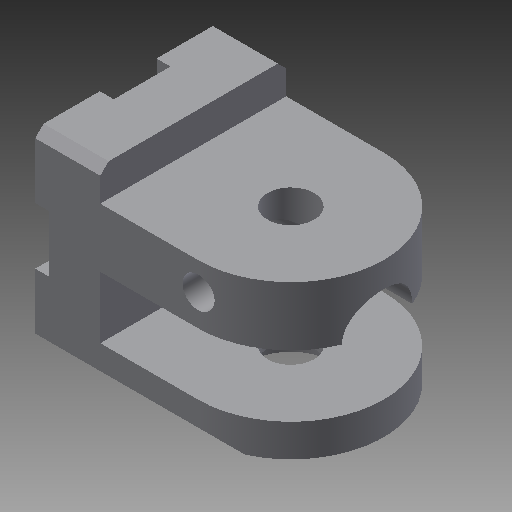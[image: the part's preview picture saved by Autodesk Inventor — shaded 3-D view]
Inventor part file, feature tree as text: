
AUTODESK INVENTOR PART (.ipt)
format: ipt  version: 2018 (Build 220112000, 112)  size: 198,656 bytes
history: native  units: mm
features: other x21, sketch x13, extrude x11, hole x2
ambient origin geometry x8: Origin, YZ Plane, XZ Plane, XY Plane, X Axis, Y Axis, Z Axis, Center Point
bodies: Solid1 (feature_tree)
feature tree (47):
  extrude  "Extrusion1"  Depth=40.0mm TaperAngle=0.0deg
  extrude  "Extrusion2"  Depth=47.5mm TaperAngle=0.0deg
  extrude  "Extrusion3"  Depth=8.4mm TaperAngle=0.0deg
  extrude  "Extrusion4"  Depth=55.0mm TaperAngle=0.0deg
  hole  "Drilling 2"  [1 undecoded]
  extrude  "Extrusion5"  Depth=10.0mm TaperAngle=0.0deg
  extrude  "Extrusion6"  [1 undecoded]
  extrude  "Extrusion7"  [1 undecoded]
  extrude  "Extrusion8"  [1 undecoded]
  extrude  "Extrusion9"  [1 undecoded]
  hole  "Drilling 3"  [1 undecoded]
  extrude  "Extrusion10"  [1 undecoded]
  extrude  "Extrusion11"  [1 undecoded]
  other  "re_XY"
  other  "re_YZ"
  other  "re_ZX"
  other  "re_X"
  other  "re_Y"
  other  "re_Z"
  other  "re_Center"
  other  "bo1_XY"
  other  "bo1_YZ"
  other  "bo1_ZX"
  other  "bo1_X"
  other  "bo1_Y"
  other  "bo1_Z"
  other  "bo1_Center"
  other  "hebel_XY"
  other  "hebel_YZ"
  other  "hebel_ZX"
  other  "hebel_X"
  other  "hebel_Y"
  other  "hebel_Z"
  other  "hebel_Center"
  sketch  "Skizze_1"  dims[d0=40.0mm d1=0.0mm d2=40.0mm d3=0.0mm]
  sketch  "Skizze_2"  dims[d4=40.0mm d5=0.0mm d6=47.5mm d7=0.0mm]
  sketch  "Skizze_3"  dims[d8=8.4mm d9=6.0mm d10=4.0mm d11=2.0mm d12=90.0deg d13=11.0mm d14=0.0mm d15=3.0mm d16=0.0mm]
  sketch  "Skizze_4"  dims[d17=55.0mm d18=0.0mm d19=55.0mm d20=0.0mm]
  sketch  "Sketch5"  dims[d21=55.0mm d22=0.0mm d23=55.0mm d24=0.0mm]
  sketch  "Skizze_6"  dims[d25=10.0mm d26=6.0mm d27=4.0mm d28=2.0mm d29=90.0deg d30=40.0mm d31=0.0mm d32=4.0mm d33=0.0mm]
  sketch  "Skizze_7"  dims[d34=20.0mm d35=0.0mm]
  sketch  "Skizze_8"
  sketch  "Skizze_9"
  sketch  "Skizze_10"
  sketch  "Sketch11"
  sketch  "Skizze_12"
  sketch  "Skizze_13"
note: 8 required parameter values undecoded (feature->parameter linkage not recoverable at this tier; creation-order binding heuristic only, values carry confidence <= 0.55)
